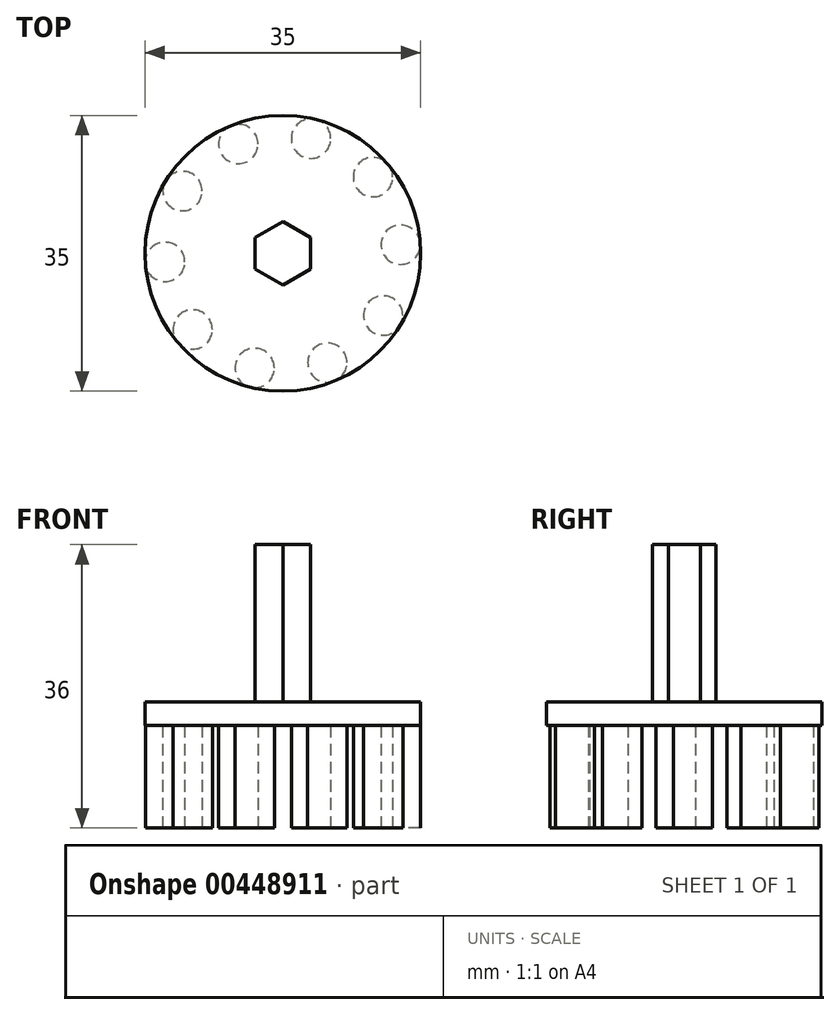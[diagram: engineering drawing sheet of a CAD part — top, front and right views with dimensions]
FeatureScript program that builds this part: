
annotation { "Feature Type Name" : "Feature", "Feature Type Description" : "" }
export const myFeature = defineFeature(function(context is Context, id is Id, definition is map)
    precondition{}
    {
        {
            var Q0;
            Q0=qCreatedBy(makeId("Top.planeOp"),FACE);
            var sketch = newSketch(context, id + "F0", { "sketchPlane" : qUnion([Q0])});
            skCircle(sketch, "E0", {"center": v(0, 0) * mm, "radius": 15 * mm});
            skCircle(sketch, "E1", {"center": v(11.46, 9.68) * mm, "radius": 2.5 * mm});
            skCircle(sketch, "E2.1.0", {"center": v(14.96, 1.1) * mm, "radius": 2.5 * mm});
            skCircle(sketch, "E2.2.0", {"center": v(12.75, -7.9) * mm, "radius": 2.5 * mm});
            skCircle(sketch, "E2.3.0", {"center": v(5.66, -13.89) * mm, "radius": 2.5 * mm});
            skCircle(sketch, "E2.4.0", {"center": v(-3.58, -14.57) * mm, "radius": 2.5 * mm});
            skCircle(sketch, "E2.5.0", {"center": v(-11.46, -9.68) * mm, "radius": 2.5 * mm});
            skCircle(sketch, "E2.6.0", {"center": v(-14.96, -1.1) * mm, "radius": 2.5 * mm});
            skCircle(sketch, "E2.7.0", {"center": v(-12.75, 7.9) * mm, "radius": 2.5 * mm});
            skCircle(sketch, "E2.8.0", {"center": v(-5.66, 13.89) * mm, "radius": 2.5 * mm});
            skCircle(sketch, "E2.9.0", {"center": v(3.58, 14.57) * mm, "radius": 2.5 * mm});
            skLineSegment(sketch, "E2.anchor1", {"start": v(0, 0) * mm, "end": v(11.46, 9.68) * mm, "construction": true});
            skLineSegment(sketch, "E2.anchor2", {"start": v(0, 0) * mm, "end": v(3.58, 14.57) * mm, "construction": true});
            skSolve(sketch);
        }
        {
            var Q0;
            {var subQ0=sQuery(id+"F0.wireOp",EDGE,"E2.8.0");var subQ1=sQuery(id+"F0.wireOp",EDGE,"E0");var subQ2=makeQuery(id+"F0.imprint","INTERSECT",VERTEX,{"disambiguationData":[OD(0.0)],"derivedFrom":[subQ1,subQ0]});Q0=makeQuery(id+"F0.imprint","IMPRINT",FACE,{"disambiguationData":[TD([[makeQuery(id+"F0.imprint","IMPRINT",EDGE,{"disambiguationData":[TD([[subQ2,-1.0]])],"derivedFrom":subQ1}),-1.0]])]});}
            var Q1;
            {var subQ0=sQuery(id+"F0.wireOp",EDGE,"E2.8.0");var subQ1=sQuery(id+"F0.wireOp",EDGE,"E0");var subQ2=makeQuery(id+"F0.imprint","INTERSECT",VERTEX,{"disambiguationData":[OD(0.0)],"derivedFrom":[subQ1,subQ0]});Q1=makeQuery(id+"F0.imprint","IMPRINT",FACE,{"disambiguationData":[TD([[makeQuery(id+"F0.imprint","IMPRINT",EDGE,{"disambiguationData":[TD([[subQ2,-1.0]])],"derivedFrom":subQ1}),1.0]])]});}
            var Q2;
            {var subQ0=sQuery(id+"F0.wireOp",EDGE,"E2.9.0");var subQ1=sQuery(id+"F0.wireOp",EDGE,"E0");var subQ2=makeQuery(id+"F0.imprint","INTERSECT",VERTEX,{"disambiguationData":[OD(0.0)],"derivedFrom":[subQ1,subQ0]});Q2=makeQuery(id+"F0.imprint","IMPRINT",FACE,{"disambiguationData":[TD([[makeQuery(id+"F0.imprint","IMPRINT",EDGE,{"disambiguationData":[TD([[subQ2,-1.0]])],"derivedFrom":subQ1}),-1.0]])]});}
            var Q3;
            {var subQ0=sQuery(id+"F0.wireOp",EDGE,"E2.9.0");var subQ1=sQuery(id+"F0.wireOp",EDGE,"E0");var subQ2=makeQuery(id+"F0.imprint","INTERSECT",VERTEX,{"disambiguationData":[OD(0.0)],"derivedFrom":[subQ1,subQ0]});Q3=makeQuery(id+"F0.imprint","IMPRINT",FACE,{"disambiguationData":[TD([[makeQuery(id+"F0.imprint","IMPRINT",EDGE,{"disambiguationData":[TD([[subQ2,-1.0]])],"derivedFrom":subQ1}),1.0]])]});}
            var Q4;
            {var subQ0=sQuery(id+"F0.wireOp",EDGE,"E1");var subQ1=sQuery(id+"F0.wireOp",EDGE,"E0");var subQ2=makeQuery(id+"F0.imprint","INTERSECT",VERTEX,{"disambiguationData":[OD(0.0)],"derivedFrom":[subQ1,subQ0]});Q4=makeQuery(id+"F0.imprint","IMPRINT",FACE,{"disambiguationData":[TD([[makeQuery(id+"F0.imprint","IMPRINT",EDGE,{"disambiguationData":[TD([[subQ2,-1.0]])],"derivedFrom":subQ1}),1.0]])]});}
            var Q5;
            {var subQ0=sQuery(id+"F0.wireOp",EDGE,"E1");var subQ1=sQuery(id+"F0.wireOp",EDGE,"E0");var subQ2=makeQuery(id+"F0.imprint","INTERSECT",VERTEX,{"disambiguationData":[OD(0.0)],"derivedFrom":[subQ1,subQ0]});Q5=makeQuery(id+"F0.imprint","IMPRINT",FACE,{"disambiguationData":[TD([[makeQuery(id+"F0.imprint","IMPRINT",EDGE,{"disambiguationData":[TD([[subQ2,-1.0]])],"derivedFrom":subQ1}),-1.0]])]});}
            var Q6;
            {var subQ0=sQuery(id+"F0.wireOp",EDGE,"E2.1.0");var subQ1=sQuery(id+"F0.wireOp",EDGE,"E0");var subQ2=makeQuery(id+"F0.imprint","INTERSECT",VERTEX,{"disambiguationData":[OD(0.0)],"derivedFrom":[subQ1,subQ0]});Q6=makeQuery(id+"F0.imprint","IMPRINT",FACE,{"disambiguationData":[TD([[makeQuery(id+"F0.imprint","IMPRINT",EDGE,{"disambiguationData":[TD([[subQ2,1.0]])],"derivedFrom":subQ1}),1.0]])]});}
            var Q7;
            {var subQ0=sQuery(id+"F0.wireOp",EDGE,"E2.1.0");var subQ1=sQuery(id+"F0.wireOp",EDGE,"E0");var subQ2=makeQuery(id+"F0.imprint","INTERSECT",VERTEX,{"disambiguationData":[OD(0.0)],"derivedFrom":[subQ1,subQ0]});Q7=makeQuery(id+"F0.imprint","IMPRINT",FACE,{"disambiguationData":[TD([[makeQuery(id+"F0.imprint","IMPRINT",EDGE,{"disambiguationData":[TD([[subQ2,1.0]])],"derivedFrom":subQ1}),-1.0]])]});}
            var Q8;
            {var subQ0=sQuery(id+"F0.wireOp",EDGE,"E2.2.0");var subQ1=sQuery(id+"F0.wireOp",EDGE,"E0");var subQ2=makeQuery(id+"F0.imprint","INTERSECT",VERTEX,{"disambiguationData":[OD(0.0)],"derivedFrom":[subQ1,subQ0]});Q8=makeQuery(id+"F0.imprint","IMPRINT",FACE,{"disambiguationData":[TD([[makeQuery(id+"F0.imprint","IMPRINT",EDGE,{"disambiguationData":[TD([[subQ2,-1.0]])],"derivedFrom":subQ1}),1.0]])]});}
            var Q9;
            {var subQ0=sQuery(id+"F0.wireOp",EDGE,"E2.2.0");var subQ1=sQuery(id+"F0.wireOp",EDGE,"E0");var subQ2=makeQuery(id+"F0.imprint","INTERSECT",VERTEX,{"disambiguationData":[OD(0.0)],"derivedFrom":[subQ1,subQ0]});Q9=makeQuery(id+"F0.imprint","IMPRINT",FACE,{"disambiguationData":[TD([[makeQuery(id+"F0.imprint","IMPRINT",EDGE,{"disambiguationData":[TD([[subQ2,-1.0]])],"derivedFrom":subQ1}),-1.0]])]});}
            var Q10;
            {var subQ0=sQuery(id+"F0.wireOp",EDGE,"E2.3.0");var subQ1=sQuery(id+"F0.wireOp",EDGE,"E0");var subQ2=makeQuery(id+"F0.imprint","INTERSECT",VERTEX,{"disambiguationData":[OD(0.0)],"derivedFrom":[subQ1,subQ0]});Q10=makeQuery(id+"F0.imprint","IMPRINT",FACE,{"disambiguationData":[TD([[makeQuery(id+"F0.imprint","IMPRINT",EDGE,{"disambiguationData":[TD([[subQ2,-1.0]])],"derivedFrom":subQ1}),1.0]])]});}
            var Q11;
            {var subQ0=sQuery(id+"F0.wireOp",EDGE,"E2.3.0");var subQ1=sQuery(id+"F0.wireOp",EDGE,"E0");var subQ2=makeQuery(id+"F0.imprint","INTERSECT",VERTEX,{"disambiguationData":[OD(0.0)],"derivedFrom":[subQ1,subQ0]});Q11=makeQuery(id+"F0.imprint","IMPRINT",FACE,{"disambiguationData":[TD([[makeQuery(id+"F0.imprint","IMPRINT",EDGE,{"disambiguationData":[TD([[subQ2,-1.0]])],"derivedFrom":subQ1}),-1.0]])]});}
            var Q12;
            {var subQ0=sQuery(id+"F0.wireOp",EDGE,"E2.4.0");var subQ1=sQuery(id+"F0.wireOp",EDGE,"E0");var subQ2=makeQuery(id+"F0.imprint","INTERSECT",VERTEX,{"disambiguationData":[OD(0.0)],"derivedFrom":[subQ1,subQ0]});Q12=makeQuery(id+"F0.imprint","IMPRINT",FACE,{"disambiguationData":[TD([[makeQuery(id+"F0.imprint","IMPRINT",EDGE,{"disambiguationData":[TD([[subQ2,-1.0]])],"derivedFrom":subQ1}),-1.0]])]});}
            var Q13;
            {var subQ0=sQuery(id+"F0.wireOp",EDGE,"E2.4.0");var subQ1=sQuery(id+"F0.wireOp",EDGE,"E0");var subQ2=makeQuery(id+"F0.imprint","INTERSECT",VERTEX,{"disambiguationData":[OD(0.0)],"derivedFrom":[subQ1,subQ0]});Q13=makeQuery(id+"F0.imprint","IMPRINT",FACE,{"disambiguationData":[TD([[makeQuery(id+"F0.imprint","IMPRINT",EDGE,{"disambiguationData":[TD([[subQ2,-1.0]])],"derivedFrom":subQ1}),1.0]])]});}
            var Q14;
            {var subQ0=sQuery(id+"F0.wireOp",EDGE,"E2.5.0");var subQ1=sQuery(id+"F0.wireOp",EDGE,"E0");var subQ2=makeQuery(id+"F0.imprint","INTERSECT",VERTEX,{"disambiguationData":[OD(0.0)],"derivedFrom":[subQ1,subQ0]});Q14=makeQuery(id+"F0.imprint","IMPRINT",FACE,{"disambiguationData":[TD([[makeQuery(id+"F0.imprint","IMPRINT",EDGE,{"disambiguationData":[TD([[subQ2,-1.0]])],"derivedFrom":subQ1}),-1.0]])]});}
            var Q15;
            {var subQ0=sQuery(id+"F0.wireOp",EDGE,"E2.5.0");var subQ1=sQuery(id+"F0.wireOp",EDGE,"E0");var subQ2=makeQuery(id+"F0.imprint","INTERSECT",VERTEX,{"disambiguationData":[OD(0.0)],"derivedFrom":[subQ1,subQ0]});Q15=makeQuery(id+"F0.imprint","IMPRINT",FACE,{"disambiguationData":[TD([[makeQuery(id+"F0.imprint","IMPRINT",EDGE,{"disambiguationData":[TD([[subQ2,-1.0]])],"derivedFrom":subQ1}),1.0]])]});}
            var Q16;
            {var subQ0=sQuery(id+"F0.wireOp",EDGE,"E2.6.0");var subQ1=sQuery(id+"F0.wireOp",EDGE,"E0");var subQ2=makeQuery(id+"F0.imprint","INTERSECT",VERTEX,{"disambiguationData":[OD(0.0)],"derivedFrom":[subQ1,subQ0]});Q16=makeQuery(id+"F0.imprint","IMPRINT",FACE,{"disambiguationData":[TD([[makeQuery(id+"F0.imprint","IMPRINT",EDGE,{"disambiguationData":[TD([[subQ2,-1.0]])],"derivedFrom":subQ1}),-1.0]])]});}
            var Q17;
            {var subQ0=sQuery(id+"F0.wireOp",EDGE,"E2.6.0");var subQ1=sQuery(id+"F0.wireOp",EDGE,"E0");var subQ2=makeQuery(id+"F0.imprint","INTERSECT",VERTEX,{"disambiguationData":[OD(0.0)],"derivedFrom":[subQ1,subQ0]});Q17=makeQuery(id+"F0.imprint","IMPRINT",FACE,{"disambiguationData":[TD([[makeQuery(id+"F0.imprint","IMPRINT",EDGE,{"disambiguationData":[TD([[subQ2,-1.0]])],"derivedFrom":subQ1}),1.0]])]});}
            var Q18;
            {var subQ0=sQuery(id+"F0.wireOp",EDGE,"E2.7.0");var subQ1=sQuery(id+"F0.wireOp",EDGE,"E0");var subQ2=makeQuery(id+"F0.imprint","INTERSECT",VERTEX,{"disambiguationData":[OD(0.0)],"derivedFrom":[subQ1,subQ0]});Q18=makeQuery(id+"F0.imprint","IMPRINT",FACE,{"disambiguationData":[TD([[makeQuery(id+"F0.imprint","IMPRINT",EDGE,{"disambiguationData":[TD([[subQ2,-1.0]])],"derivedFrom":subQ1}),-1.0]])]});}
            var Q19;
            {var subQ0=sQuery(id+"F0.wireOp",EDGE,"E2.7.0");var subQ1=sQuery(id+"F0.wireOp",EDGE,"E0");var subQ2=makeQuery(id+"F0.imprint","INTERSECT",VERTEX,{"disambiguationData":[OD(0.0)],"derivedFrom":[subQ1,subQ0]});Q19=makeQuery(id+"F0.imprint","IMPRINT",FACE,{"disambiguationData":[TD([[makeQuery(id+"F0.imprint","IMPRINT",EDGE,{"disambiguationData":[TD([[subQ2,-1.0]])],"derivedFrom":subQ1}),1.0]])]});}
            extrude(context, id + "F1", {"entities" : qUnion([Q0, Q1, Q2, Q3, Q4, Q5, Q6, Q7, Q8, Q9, Q10, Q11, Q12, Q13, Q14, Q15, Q16, Q17, Q18, Q19]), "depth" : 13 * mm});
        }
        {
            var Q0;
            Q0=makeQuery(id+"F1.opExtrude","CAP_FACE",FACE,{"disambiguationData":[OSD([sQuery(id+"F0.wireOp",EDGE,"E2.3.0")])],"isStart":false});
            var sketch = newSketch(context, id + "F2", { "sketchPlane" : qUnion([Q0])});
            skPoint(sketch, "E3.0", {"position": v(0, 0) * mm});
            skCircle(sketch, "E4", {"center": v(0, 0) * mm, "radius": 17.5 * mm});
            skSolve(sketch);
        }
        {
            var Q0;
            Q0=makeQuery(id+"F2.imprint","IMPRINT",FACE,{"disambiguationData":[TD([[makeQuery(id+"F2.imprint","IMPRINT",EDGE,{"derivedFrom":sQuery(id+"F2.wireOp",EDGE,"E4")}),1.0]])]});
            var Q1;
            Q1=makeQuery(id+"F2.imprint","IMPRINT",FACE,{"disambiguationData":[TD([[makeQuery(id+"F2.imprint","IMPRINT",EDGE,{"derivedFrom":makeQuery(id+"F1.opExtrude","CAP_EDGE",EDGE,{"disambiguationData":[OSD([sQuery(id+"F0.wireOp",EDGE,"E2.3.0")])],"isStart":false})}),1.0]])]});
            extrude(context, id + "F3", {"entities" : qUnion([Q0, Q1]), "depth" : 3 * mm});
        }
        {
            var Q0;
            Q0=makeQuery(id+"F3.opExtrude","CAP_FACE",FACE,{"disambiguationData":[OSD([sQuery(id+"F2.wireOp",EDGE,"E4")])],"isStart":false});
            var sketch = newSketch(context, id + "F4", { "sketchPlane" : qUnion([Q0])});
            skCircle(sketch, "E5.cCircle", {"center": v(0, 0) * mm, "radius": 3.5 * mm, "construction": true});
            skLineSegment(sketch, "E5.0", {"start": v(3.5, 2.02) * mm, "end": v(3.5, -2.02) * mm});
            skLineSegment(sketch, "E5.1", {"start": v(3.5, -2.02) * mm, "end": v(0, -4.04) * mm});
            skLineSegment(sketch, "E5.2", {"start": v(0, -4.04) * mm, "end": v(-3.5, -2.02) * mm});
            skLineSegment(sketch, "E5.3", {"start": v(-3.5, -2.02) * mm, "end": v(-3.5, 2.02) * mm});
            skLineSegment(sketch, "E5.4", {"start": v(-3.5, 2.02) * mm, "end": v(0, 4.04) * mm});
            skLineSegment(sketch, "E5.5", {"start": v(0, 4.04) * mm, "end": v(3.5, 2.02) * mm});
            skPoint(sketch, "E5.0.midPoint", {"position": v(3.5, 0) * mm});
            skSolve(sketch);
        }
        {
            var Q0;
            Q0=makeQuery(id+"F4.imprint","IMPRINT",FACE,{"disambiguationData":[TD([[makeQuery(id+"F4.imprint","IMPRINT",EDGE,{"derivedFrom":sQuery(id+"F4.wireOp",EDGE,"E5.0")}),-1.0]])]});
            extrude(context, id + "F5", {"entities" : qUnion([Q0]), "operationType" : NewBodyOperationType.ADD, "depth" : 20 * mm});
        }
    });
